# Revit family: Basin_Prepackaged_System-Indoor-Zoeller-18x30-912_Series
name_source: partatom
category: Mechanical Equipment
revit_build: Autodesk Revit 2014 (Build: 20130308_1515(x64)
units: mm (PartAtom-declared; Revit-internal decimal feet)

## types (4) — shared parameters
Assembly Code = D2030400
Basin Type = Polythylene Structural Foam (PSF)
CW Connection = Yes
Cooling = Oil Filled
Cord Length = 180"
Default Elevation = 0"
Description = 912 Indoor Package Systems.
Diameter = 18"
Discharge Radius = 1"
Discharge Size = 2"
HW Connection = No
Height = 30"
Hertz = 60
Inlet Diameter = 4"
Inlet Radius = 2"
Insulation = Class B
Manufacturer = Zoeller
Material = Foam-Zoeller-Poly Structural Foam (PSF)
Max. Operating Temp. = 130°F (54°C)
Model = 912-0082/M264
Motor Protection = Auto reset thermal overload
Nominal Radius = 5"
Operation = Automatic
Phase = 1
Price = Prices may vary. Please consult Manufacturer Representative for most up-to-date price list.
Product Documentation Link = http://cdn.qleapahead.com
Product Page URL = http://www.zoellerpumps.com
Pump Housing = Metal-Zoeller-Powder Coated Cast Iron
RPM = 1725
Radius = 9"
Shipping Weight = 61.00 lb
Solid Handling = 2" (50mm) spherical solids
URL = http://www.zoeller.com
Vent Connection = No
Voltage = 115 V
Waste Connection = Yes

## per-type parameters (varying)
| type | Alarm | Amps | Flow @ 5' | Type |
| 912-0005/BN264 - 912-0007/M264 - 115V, 9.4Amps, 90gpm@5' | No | 9.4 | 90 GPM | Permanent Split Capacitor |
| 912-1005/BN264 - 912-1007/M264 - 115V, 9.4Amps, 90gpm@5'/APak Alarm | Yes | 9.4 | 90 GPM | Permanent Split Capacitor |
| 912-0017/BN266 - 912-0010/M266 - 115V, 9.4Amps, 128gpm@5' | No | 10.4 | 128 GPM | Split Phase |
| 912-1017/BN266 - 912-1010/M266 - 115V, 9.4Amps, 128gpm@5'/APak Alarm | Yes | 9.4 | 128 GPM | Split Phase |

## geometry (parser evidence)
native form markers: Sweep x3
no freeform markers — native parametric forms only
